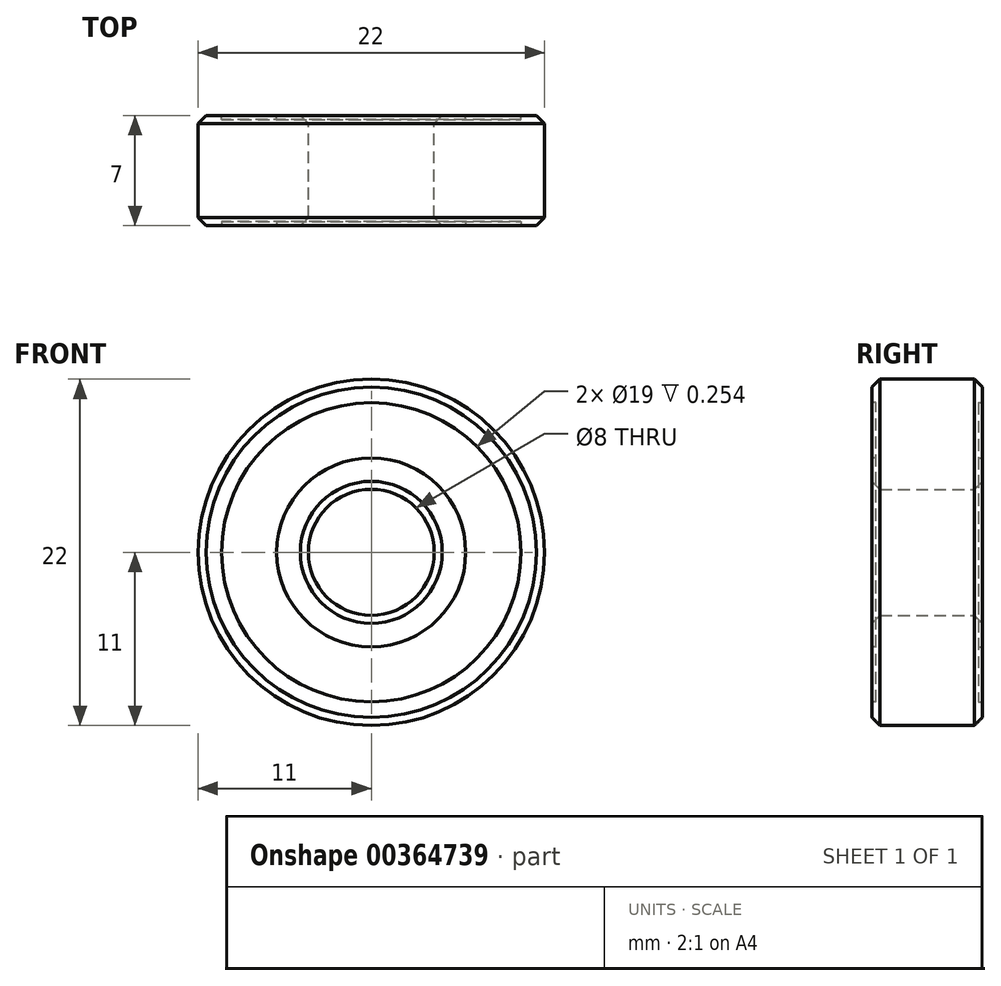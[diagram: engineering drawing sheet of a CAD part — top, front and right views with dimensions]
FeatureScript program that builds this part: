
annotation { "Feature Type Name" : "Feature", "Feature Type Description" : "" }
export const myFeature = defineFeature(function(context is Context, id is Id, definition is map)
    precondition{}
    {
        {
            var Q0;
            Q0=qCreatedBy(makeId("Front.planeOp"),FACE);
            var sketch = newSketch(context, id + "F0", { "sketchPlane" : qUnion([Q0])});
            skCircle(sketch, "E0", {"center": v(0, 0) * mm, "radius": 4 * mm});
            skCircle(sketch, "E1", {"center": v(0, 0) * mm, "radius": 11 * mm});
            skSolve(sketch);
        }
        {
            var Q0;
            Q0=qSketchRegion(id+"F0",true);
            extrude(context, id + "F1", {"entities" : qUnion([Q0]), "depth" : 7 * mm});
        }
        {
            var Q0;
            Q0=makeQuery(id+"F1.opExtrude","SWEPT_FACE",FACE,{"disambiguationData":[OSD([sQuery(id+"F0.wireOp",EDGE,"E1")])]});
            var Q1;
            Q1=makeQuery(id+"F1.opExtrude","SWEPT_FACE",FACE,{"disambiguationData":[OSD([sQuery(id+"F0.wireOp",EDGE,"E0")])]});
            chamfer(context, id + "F2", {"entities" : qUnion([Q0, Q1]), "width" : 0.5 * mm, "tangentPropagation" : true});
        }
        {
            var Q0;
            Q0=makeQuery(id+"F1.opExtrude","CAP_FACE",FACE,{"disambiguationData":[OSD([sQuery(id+"F0.wireOp",EDGE,"E0"),sQuery(id+"F0.wireOp",EDGE,"E1")])],"isStart":false});
            var sketch = newSketch(context, id + "F3", { "sketchPlane" : qUnion([Q0])});
            skCircle(sketch, "E2", {"center": v(0, 0) * mm, "radius": 6 * mm});
            skCircle(sketch, "E3", {"center": v(0, 0) * mm, "radius": 9.5 * mm});
            skSolve(sketch);
        }
        {
            var Q0;
            Q0=qSketchRegion(id+"F3",true);
            extrude(context, id + "F4", {"entities" : qUnion([Q0]), "operationType" : NewBodyOperationType.REMOVE, "oppositeDirection" : true, "depth" : 0.25 * mm});
        }
        {
            var Q0;
            Q0=makeQuery(id+"F1.opExtrude","CAP_FACE",FACE,{"disambiguationData":[OSD([sQuery(id+"F0.wireOp",EDGE,"E0"),sQuery(id+"F0.wireOp",EDGE,"E1")])],"isStart":true});
            var sketch = newSketch(context, id + "F5", { "sketchPlane" : qUnion([Q0])});
            skCircle(sketch, "E4", {"center": v(0, 0) * mm, "radius": 6 * mm});
            skCircle(sketch, "E5", {"center": v(0, 0) * mm, "radius": 9.5 * mm});
            skSolve(sketch);
        }
        {
            var Q0;
            Q0=qSketchRegion(id+"F5",true);
            extrude(context, id + "F6", {"entities" : qUnion([Q0]), "operationType" : NewBodyOperationType.REMOVE, "oppositeDirection" : true, "depth" : 0.25 * mm});
        }
    });
